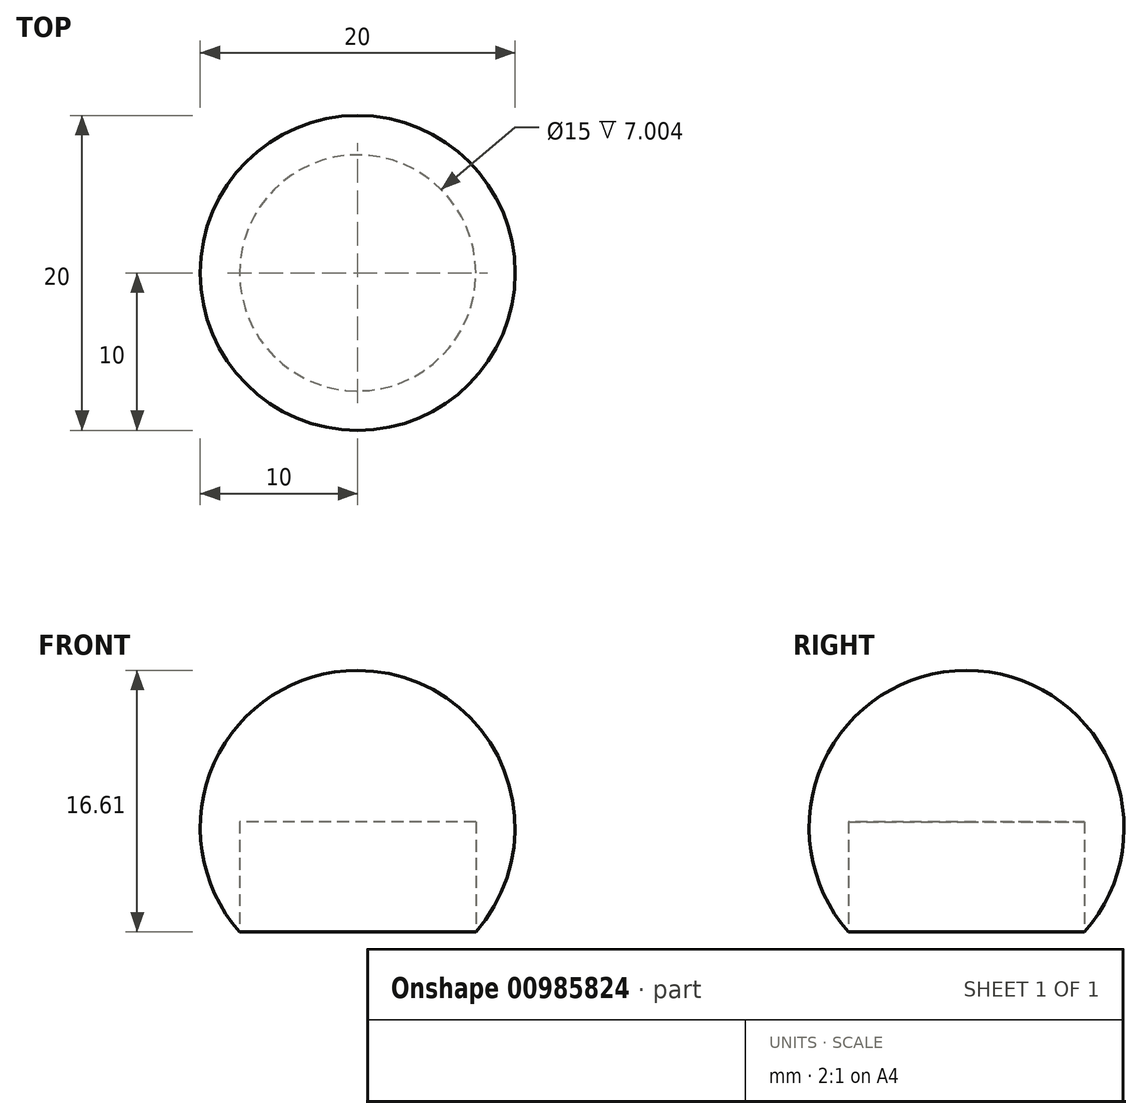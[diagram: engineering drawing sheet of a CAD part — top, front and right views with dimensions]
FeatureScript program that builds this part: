
annotation { "Feature Type Name" : "Feature", "Feature Type Description" : "" }
export const myFeature = defineFeature(function(context is Context, id is Id, definition is map)
    precondition{}
    {
        {
            var Q0;
            Q0=qCreatedBy(makeId("Top.planeOp"),FACE);
            var sketch = newSketch(context, id + "F0", { "sketchPlane" : qUnion([Q0])});
            skCircle(sketch, "E0", {"center": v(0, 0) * mm, "radius": 10 * mm});
            skSolve(sketch);
        }
        {
            var Q0;
            Q0=makeQuery(id+"F0.imprint","IMPRINT",FACE,{"disambiguationData":[TD([[makeQuery(id+"F0.imprint","IMPRINT",EDGE,{"derivedFrom":sQuery(id+"F0.wireOp",EDGE,"E0")}),1.0]])]});
            extrude(context, id + "F1", {"entities" : qUnion([Q0]), "depth" : 20 * mm, "offsetDistance" : 25 * mm});
        }
        {
            var Q0;
            Q0=makeQuery(id+"F1.opExtrude","CAP_EDGE",EDGE,{"disambiguationData":[OSD([sQuery(id+"F0.wireOp",EDGE,"E0")])],"isStart":false});
            var Q1;
            Q1=makeQuery(id+"F1.opExtrude","CAP_EDGE",EDGE,{"disambiguationData":[OSD([sQuery(id+"F0.wireOp",EDGE,"E0")])],"isStart":true});
            fillet(context, id + "F2", {"entities" : qUnion([Q0, Q1]), "radius" : 10 * mm, "tangentPropagation" : true, "allowEdgeOverflow" : false});
        }
        {
            var Q0;
            Q0=qCreatedBy(makeId("Top.planeOp"),FACE);
            var sketch = newSketch(context, id + "F3", { "sketchPlane" : qUnion([Q0])});
            skCircle(sketch, "E1", {"center": v(0, 0) * mm, "radius": 7.5 * mm});
            skSolve(sketch);
        }
        {
            var Q0;
            Q0 = qSketchRegion(id + "F3", true);
            extrude(context, id + "F4", {"entities" : qUnion([Q0]), "operationType" : NewBodyOperationType.REMOVE, "depth" : 10.4 * mm, "offsetDistance" : 25 * mm});
        }
    });
